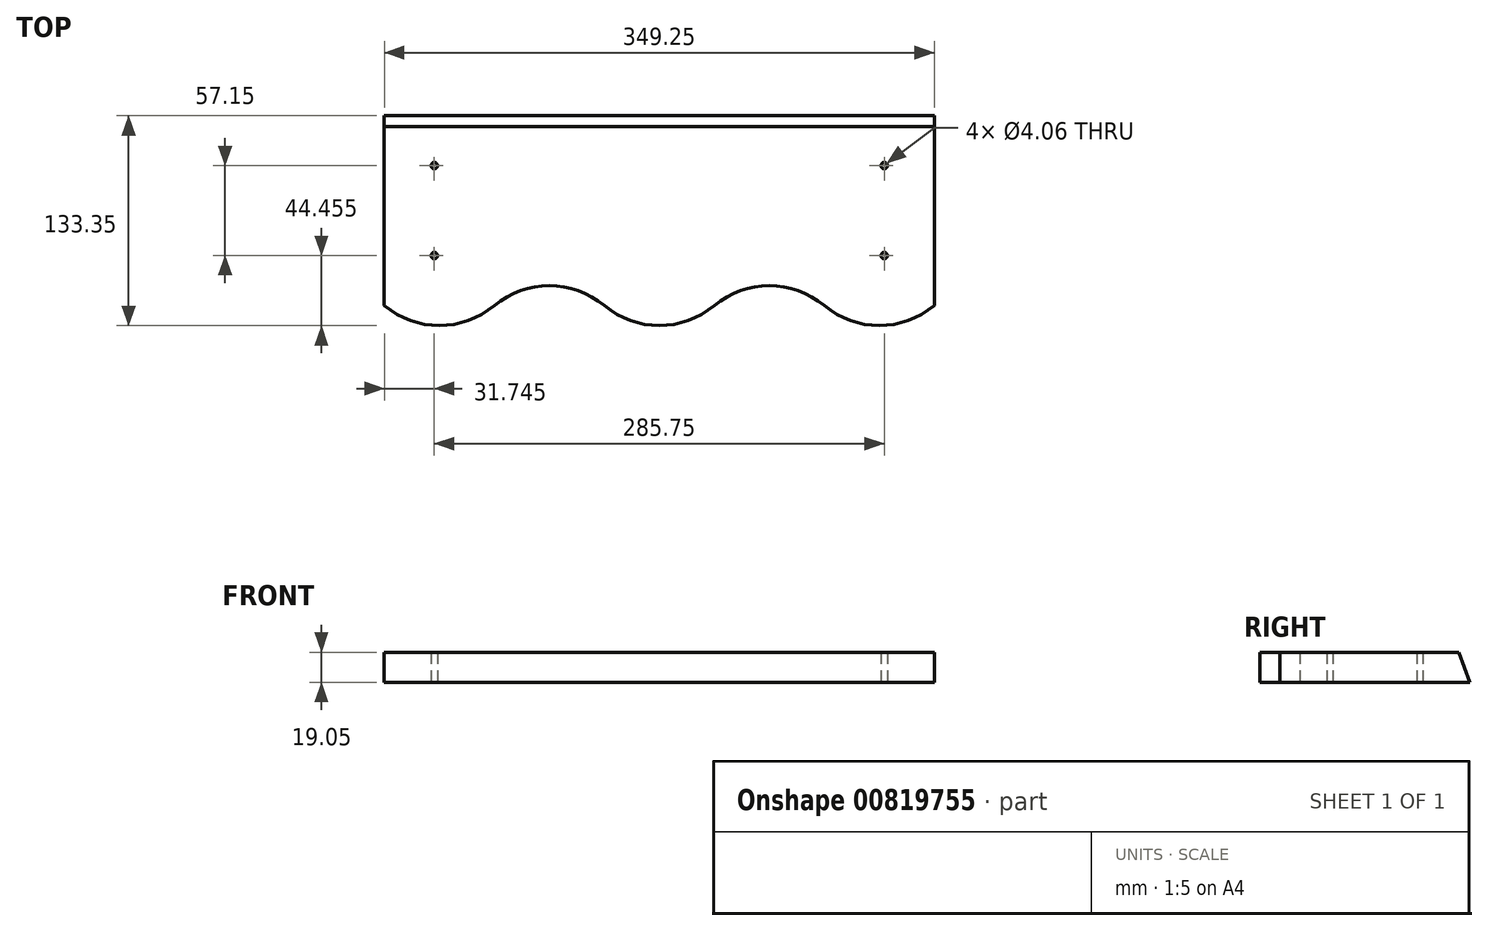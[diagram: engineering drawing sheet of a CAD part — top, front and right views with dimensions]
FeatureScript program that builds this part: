
annotation { "Feature Type Name" : "Feature", "Feature Type Description" : "" }
export const myFeature = defineFeature(function(context is Context, id is Id, definition is map)
    precondition{}
    {
        {
            var Q0;
            Q0=qCreatedBy(makeId("Top.planeOp"),FACE);
            var sketch = newSketch(context, id + "F0", { "sketchPlane" : qUnion([Q0])});
            skLineSegment(sketch, "E0.top", {"start": v(174.63, 66.68) * mm, "end": v(-174.63, 66.67) * mm});
            skLineSegment(sketch, "E0.left", {"start": v(174.63, -53.99) * mm, "end": v(174.62, 66.68) * mm});
            skLineSegment(sketch, "E0.right", {"start": v(-174.63, -53.99) * mm, "end": v(-174.63, 66.67) * mm});
            skPoint(sketch, "E0.middle", {"position": v(0, 0) * mm});
            skLineSegment(sketch, "E1", {"start": v(-104.78, 66.68) * mm, "end": v(-104.78, -66.68) * mm, "construction": true});
            skLineSegment(sketch, "E2", {"start": v(-34.93, 66.68) * mm, "end": v(-34.93, -66.68) * mm, "construction": true});
            skLineSegment(sketch, "E3", {"start": v(34.93, 66.68) * mm, "end": v(34.93, -66.68) * mm, "construction": true});
            skLineSegment(sketch, "E4", {"start": v(104.78, 66.68) * mm, "end": v(104.78, -66.67) * mm, "construction": true});
            skLineSegment(sketch, "E5", {"start": v(-174.62, -53.99) * mm, "end": v(174.63, -53.99) * mm, "construction": true});
            skArc(sketch, "E6", {"start": v(-174.62, -53.99) * mm, "mid": v(-139.7, -66.68) * mm, "end": v(-104.77, -53.99) * mm});
            skArc(sketch, "E7", {"start": v(-34.92, -53.99) * mm, "mid": v(-69.85, -41.3) * mm, "end": v(-104.78, -53.99) * mm});
            skArc(sketch, "E8", {"start": v(-34.92, -53.99) * mm, "mid": v(0, -66.68) * mm, "end": v(34.93, -53.99) * mm});
            skArc(sketch, "E9", {"start": v(104.78, -53.99) * mm, "mid": v(69.85, -41.3) * mm, "end": v(34.93, -53.99) * mm});
            skArc(sketch, "E10", {"start": v(104.78, -53.99) * mm, "mid": v(139.7, -66.68) * mm, "end": v(174.63, -53.99) * mm});
            skPoint(sketch, "E11.orphan", {"position": v(-174.63, -66.68) * mm});
            skPoint(sketch, "E12.orphan", {"position": v(174.63, -66.67) * mm});
            skLineSegment(sketch, "E13", {"start": v(-142.88, 66.67) * mm, "end": v(-142.88, -53.99) * mm, "construction": true});
            skLineSegment(sketch, "E14", {"start": v(142.88, 66.68) * mm, "end": v(142.88, -53.99) * mm, "construction": true});
            skLineSegment(sketch, "E15", {"start": v(-174.63, 34.92) * mm, "end": v(174.63, 34.93) * mm, "construction": true});
            skLineSegment(sketch, "E16", {"start": v(-174.63, -22.23) * mm, "end": v(174.62, -22.22) * mm, "construction": true});
            skCircle(sketch, "E17", {"center": v(-142.88, 34.92) * mm, "radius": 2.03 * mm});
            skCircle(sketch, "E18", {"center": v(-142.88, -22.23) * mm, "radius": 2.03 * mm});
            skCircle(sketch, "E19", {"center": v(142.87, 34.93) * mm, "radius": 2.03 * mm});
            skCircle(sketch, "E20", {"center": v(142.88, -22.22) * mm, "radius": 2.03 * mm});
            skSolve(sketch);
        }
        {
            var Q0;
            Q0=makeQuery(id+"F0.imprint","IMPRINT",FACE,{"disambiguationData":[TD([[makeQuery(id+"F0.imprint","IMPRINT",EDGE,{"derivedFrom":sQuery(id+"F0.wireOp",EDGE,"E0.top")}),1.0]])]});
            extrude(context, id + "F1", {"entities" : qUnion([Q0]), "depth" : 19.05 * mm, "offsetDistance" : 25.4 * mm});
        }
        {
            var Q0;
            Q0=makeQuery(id+"F1.opExtrude","SWEPT_FACE",FACE,{"disambiguationData":[OSD([sQuery(id+"F0.wireOp",EDGE,"E0.right")])]});
            var sketch = newSketch(context, id + "F2", { "sketchPlane" : qUnion([Q0])});
            skLineSegment(sketch, "E21", {"start": v(-66.68, 19.05) * mm, "end": v(-66.68, 0) * mm});
            skLineSegment(sketch, "E22", {"start": v(-66.68, 0) * mm, "end": v(-59.74, 19.05) * mm});
            skLineSegment(sketch, "E23", {"start": v(-59.74, 19.05) * mm, "end": v(-66.68, 19.05) * mm});
            skSolve(sketch);
        }
        {
            var Q0;
            Q0=makeQuery(id+"F2.imprint","IMPRINT",FACE,{"disambiguationData":[TD([[makeQuery(id+"F2.imprint","IMPRINT",EDGE,{"derivedFrom":sQuery(id+"F2.wireOp",EDGE,"E21")}),1.0]])]});
            extrude(context, id + "F3", {"entities" : qUnion([Q0]), "operationType" : NewBodyOperationType.REMOVE, "oppositeDirection" : true, "depth" : 349.25 * mm, "offsetDistance" : 25.4 * mm});
        }
    });
